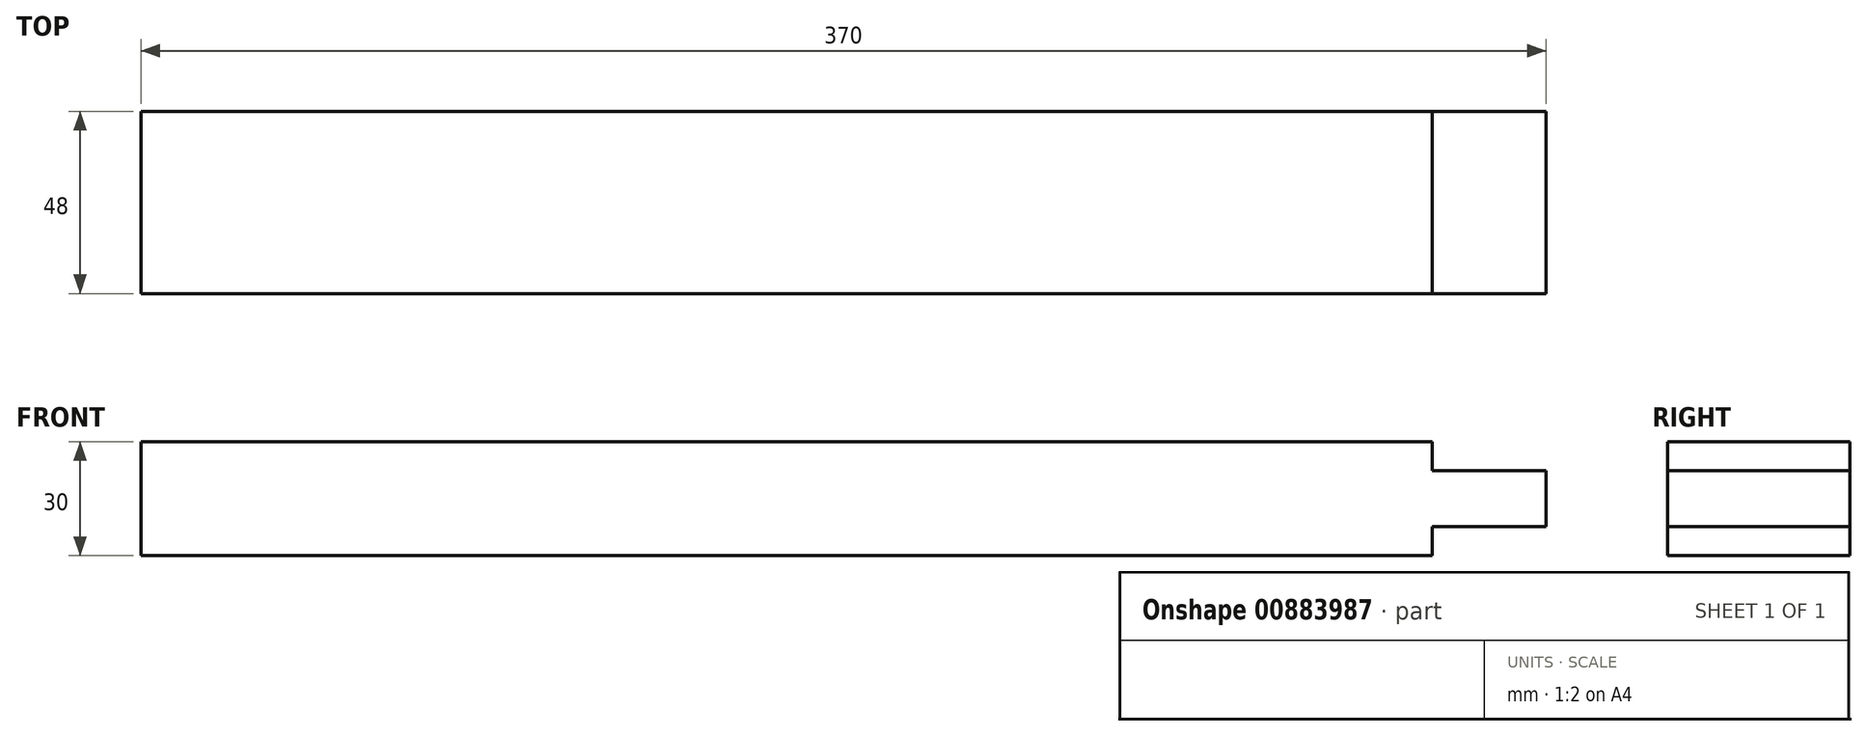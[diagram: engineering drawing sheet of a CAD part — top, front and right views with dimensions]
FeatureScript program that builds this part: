
annotation { "Feature Type Name" : "Feature", "Feature Type Description" : "" }
export const myFeature = defineFeature(function(context is Context, id is Id, definition is map)
    precondition{}
    {
        {
            var Q0;
            Q0=qCreatedBy(makeId("Top.planeOp"),FACE);
            var sketch = newSketch(context, id + "F0", { "sketchPlane" : qUnion([Q0])});
            skLineSegment(sketch, "E0.bottom", {"start": v(170, -24) * mm, "end": v(-170, -24) * mm});
            skLineSegment(sketch, "E0.top", {"start": v(170, 24) * mm, "end": v(-170, 24) * mm});
            skLineSegment(sketch, "E0.left", {"start": v(170, -24) * mm, "end": v(170, 24) * mm});
            skLineSegment(sketch, "E0.right", {"start": v(-170, -24) * mm, "end": v(-170, 24) * mm});
            skPoint(sketch, "E0.middle", {"position": v(0, 0) * mm});
            skSolve(sketch);
        }
        {
            var Q0;
            Q0=makeQuery(id+"F0.imprint","IMPRINT",FACE,{"disambiguationData":[TD([[makeQuery(id+"F0.imprint","IMPRINT",EDGE,{"derivedFrom":sQuery(id+"F0.wireOp",EDGE,"E0.bottom")}),-1.0]])]});
            extrude(context, id + "F1", {"entities" : qUnion([Q0]), "depth" : 30 * mm, "offsetDistance" : 25 * mm});
        }
        {
            var Q0;
            Q0=makeQuery(id+"F1.opExtrude","SWEPT_FACE",FACE,{"disambiguationData":[OSD([sQuery(id+"F0.wireOp",EDGE,"E0.left")])]});
            var sketch = newSketch(context, id + "F2", { "sketchPlane" : qUnion([Q0])});
            skLineSegment(sketch, "E1", {"start": v(24, 0) * mm, "end": v(-24, 0) * mm});
            skLineSegment(sketch, "E2.bottom", {"start": v(-24, 7.67) * mm, "end": v(24, 7.67) * mm});
            skLineSegment(sketch, "E2.top", {"start": v(-24, 22.33) * mm, "end": v(24, 22.33) * mm});
            skLineSegment(sketch, "E2.left", {"start": v(-24, 7.67) * mm, "end": v(-24, 22.33) * mm});
            skLineSegment(sketch, "E2.right", {"start": v(24, 7.67) * mm, "end": v(24, 22.33) * mm});
            skPoint(sketch, "E2.middle", {"position": v(0, 15) * mm});
            skSolve(sketch);
        }
        {
            var Q0;
            Q0 = qSketchRegion(id + "F2", true);
            extrude(context, id + "F3", {"entities" : qUnion([Q0]), "operationType" : NewBodyOperationType.ADD, "depth" : 30 * mm, "offsetDistance" : 25 * mm});
        }
    });
